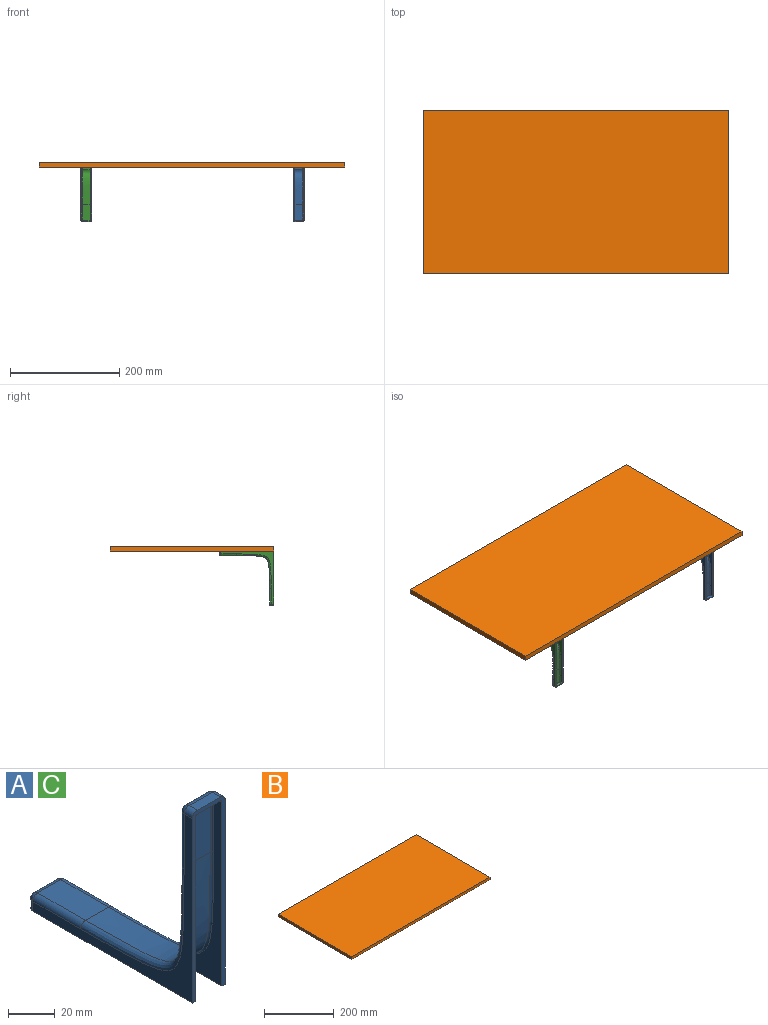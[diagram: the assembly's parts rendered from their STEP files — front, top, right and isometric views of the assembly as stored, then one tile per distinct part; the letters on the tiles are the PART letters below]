
ASSEMBLY  parts=3 mates=4
PART A: 48 faces, bbox 26x104x104 mm
  f0: plane 100x20mm, normal (0,0,-1), area 428.6mm2, adj f1,f2,f6,f7,f16,f21,f25,f29
  f1: plane 100x20mm, normal (0,-1,0), area 428.6mm2, adj f0,f5,f6,f7,f9,f13,f28,f29
  f2: plane 14x5mm, normal (0,1,0), area 70mm2, adj f0,f16,f20,f21
  f3: plane 29x14mm, normal (0,0,1), area 406mm2, adj f8,f15,f20,f24
  f4: plane 29x14mm, normal (0,1,0), area 406mm2, adj f8,f10,f14,f19
  f5: plane 14x5mm, normal (0,0,1), area 70mm2, adj f1,f9,f13,f14
  f6: plane 97x97mm, normal (1,0,0), area 1111.9mm2, adj f0,f1,f13,f19,f21,f22,f24
  f7: plane 97x97mm, normal (-1,0,0), area 1111.9mm2, adj f0,f1,f9,f10,f12,f15,f16
  f8: bspline ~60x60mm, area 1543mm2, adj f3,f4,f12,f22
  f9: cylinder r=3mm len=5mm, axis (0,-1,0), area 23.6mm2, adj f1,f5,f7,f11
  f10: cylinder r=3mm len=29mm, axis (0,0,1), area 136.7mm2, adj f4,f7,f11,f12
  f11: sphere r=3mm, area 16.7mm2, adj f9,f10,f14
  f12: bspline ~73.14x73.14mm, area 527.5mm2, adj f7,f8,f10,f15
  f13: cylinder r=3mm len=5mm, axis (0,1,0), area 23.6mm2, adj f1,f5,f6,f17
  f14: cylinder r=3mm len=14mm, axis (-1,0,0), area 66mm2, adj f4,f5,f11,f17
  f15: cylinder r=3mm len=29mm, axis (0,-1,0), area 136.7mm2, adj f3,f7,f12,f18
  f16: cylinder r=3mm len=5mm, axis (0,0,1), area 23.6mm2, adj f0,f2,f7,f18
  f17: sphere r=3mm, area 14.1mm2, adj f13,f14,f19
  f18: sphere r=3mm, area 14.1mm2, adj f15,f16,f20
  f19: cylinder r=3mm len=29mm, axis (0,0,-1), area 136.7mm2, adj f4,f6,f17,f22
  f20: cylinder r=3mm len=14mm, axis (-1,0,0), area 66mm2, adj f2,f3,f18,f23
  f21: cylinder r=3mm len=5mm, axis (0,0,-1), area 23.6mm2, adj f0,f2,f6,f23
  f22: bspline ~73.14x73.14mm, area 527.5mm2, adj f6,f8,f19,f24
  f23: sphere r=3mm, area 14.1mm2, adj f20,f21,f24
  f24: cylinder r=3mm len=29mm, axis (0,1,0), area 136.7mm2, adj f3,f6,f22,f23
  f25: plane 14x5mm, normal (0,-1,0), area 70mm2, adj f0,f39,f43,f44
  f26: plane 29x14mm, normal (0,0,-1), area 406mm2, adj f31,f38,f43,f47
  f27: plane 29x14mm, normal (0,-1,0), area 406mm2, adj f31,f33,f37,f42
  f28: plane 14x5mm, normal (0,0,-1), area 70mm2, adj f1,f32,f36,f37
  f29: plane 97x97mm, normal (-1,0,0), area 1111.9mm2, adj f0,f1,f36,f42,f44,f45,f47
  f30: plane 97x97mm, normal (1,0,0), area 1111.9mm2, adj f0,f1,f32,f33,f35,f38,f39
  f31: offset ~64x64mm, area 1587.2mm2, adj f26,f27,f35,f45
  f32: cylinder r=1mm len=5mm, axis (0,-1,0), area 7.9mm2, adj f1,f28,f30,f34
  f33: cylinder r=1mm len=29mm, axis (0,0,1), area 45.6mm2, adj f27,f30,f34,f35
  f34: sphere r=1mm, area 2.1mm2, adj f32,f33,f37
  f35: bspline ~73.14x73.14mm, area 179mm2, adj f30,f31,f33,f38
  f36: cylinder r=1mm len=5mm, axis (0,1,0), area 7.9mm2, adj f1,f28,f29,f40
  f37: cylinder r=1mm len=14mm, axis (-1,0,0), area 22mm2, adj f27,f28,f34,f40
  f38: cylinder r=1mm len=29mm, axis (0,-1,0), area 45.6mm2, adj f26,f30,f35,f41
  f39: cylinder r=1mm len=5mm, axis (0,0,1), area 7.9mm2, adj f0,f25,f30,f41
  f40: sphere r=1mm, area 1mm2, adj f36,f37,f42
  f41: sphere r=1mm, area 2.1mm2, adj f38,f39,f43
  f42: cylinder r=1mm len=29mm, axis (0,0,-1), area 45.6mm2, adj f27,f29,f40,f45
  f43: cylinder r=1mm len=14mm, axis (-1,0,0), area 22mm2, adj f25,f26,f41,f46
  f44: cylinder r=1mm len=5mm, axis (0,0,-1), area 7.9mm2, adj f0,f25,f29,f46
  f45: bspline ~73.14x73.14mm, area 179mm2, adj f29,f31,f42,f47
  f46: sphere r=1mm, area 1mm2, adj f43,f44,f47
  f47: cylinder r=1mm len=29mm, axis (0,1,0), area 45.6mm2, adj f26,f29,f45,f46
PART B: 6 faces, bbox 560x300x9 mm
  f0: plane 300x9mm, normal (-1,0,0), area 2700mm2, adj f1,f3,f4,f5
  f1: plane 560x9mm, normal (0,-1,0), area 5040mm2, adj f0,f2,f4,f5
  f2: plane 300x9mm, normal (1,0,0), area 2700mm2, adj f1,f3,f4,f5
  f3: plane 560x9mm, normal (0,1,0), area 5040mm2, adj f0,f2,f4,f5
  f4: plane 560x300mm, normal (0,0,1), area 168000mm2, adj f0,f1,f2,f3
  f5: plane 560x300mm, normal (0,0,-1), area 168000mm2, adj f0,f1,f2,f3
PART C: same geometry as A
PLACE A rot(axis=(-1,0,0),90deg) t=(629.59,203.76,954.48)mm
PLACE B rot(axis=(1,0,0),180deg) t=(164.08,503.76,963.48)mm
PLACE C rot(axis=(0,-1,0),180deg) t=(260.5,203.76,954.48)mm
MATE planar B.f3 <-> A.f0  axis (0,-1,0) through (444.08,203.76,958.98)mm
MATE planar C.f0 <-> B.f4  axis (0,0,1) through (250.5,257.02,954.48)mm
MATE planar A.f1 <-> B.f4  axis (0,0,1) through (639.59,257.02,954.48)mm
MATE planar C.f1 <-> B.f3  axis (0,-1,0) through (250.5,203.76,901.21)mm
